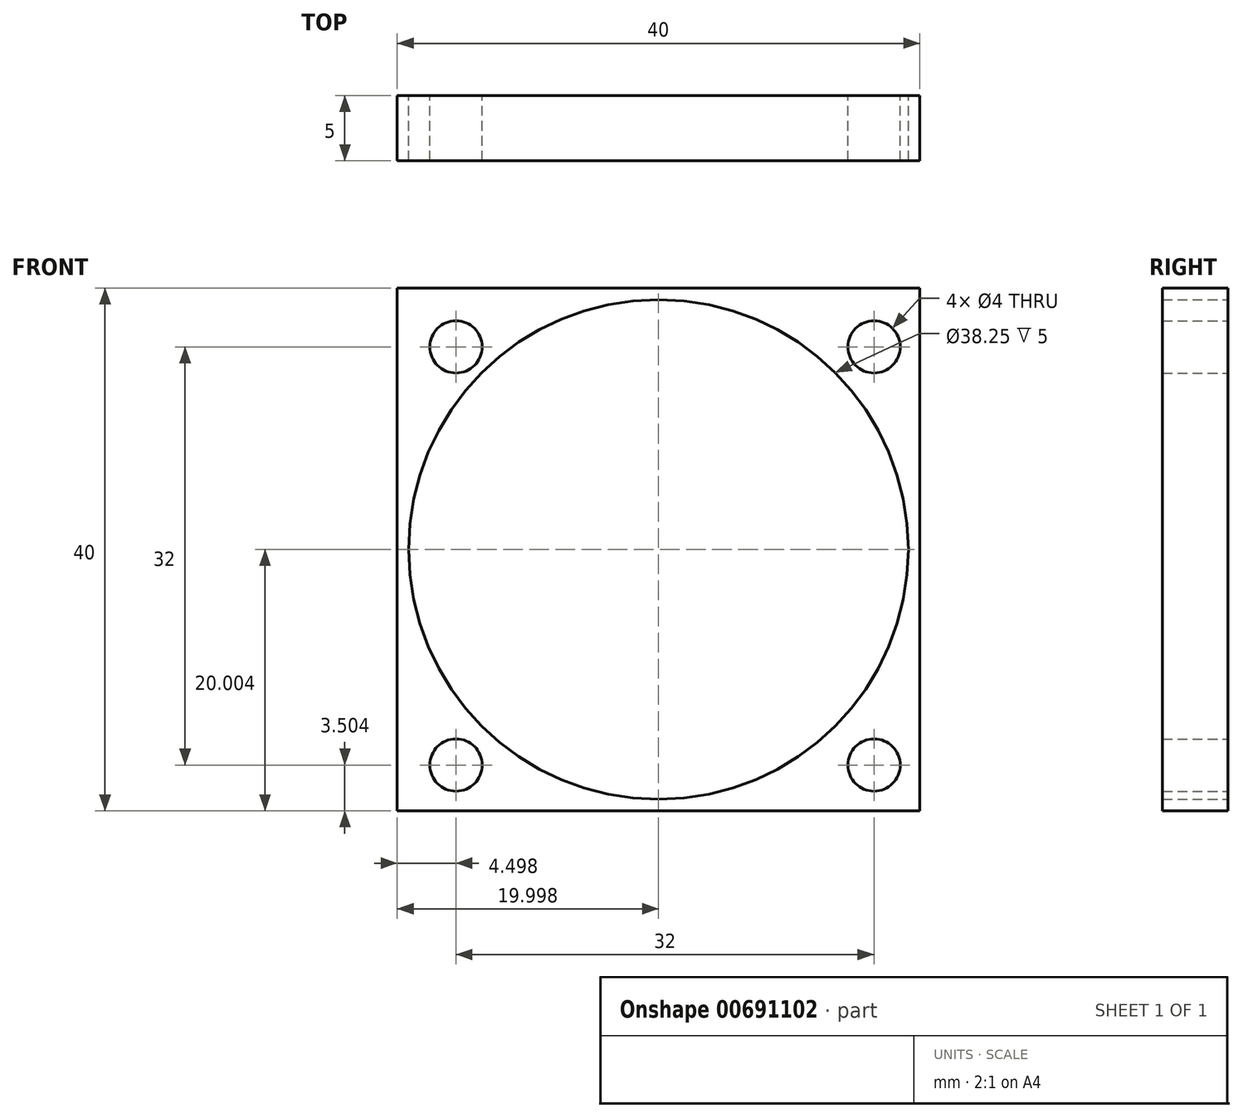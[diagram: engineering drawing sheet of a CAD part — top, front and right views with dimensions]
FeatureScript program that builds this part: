
annotation { "Feature Type Name" : "Feature", "Feature Type Description" : "" }
export const myFeature = defineFeature(function(context is Context, id is Id, definition is map)
    precondition{}
    {
        {
            var Q0;
            Q0=qCreatedBy(makeId("Front.planeOp"),FACE);
            var sketch = newSketch(context, id + "F0", { "sketchPlane" : qUnion([Q0])});
            skLineSegment(sketch, "E0.bottom", {"start": v(-27.87, 25.17) * mm, "end": v(12.13, 25.17) * mm});
            skLineSegment(sketch, "E0.top", {"start": v(-27.87, -14.83) * mm, "end": v(12.13, -14.83) * mm});
            skLineSegment(sketch, "E0.left", {"start": v(-27.87, 25.17) * mm, "end": v(-27.87, -14.83) * mm});
            skLineSegment(sketch, "E0.right", {"start": v(12.13, 25.17) * mm, "end": v(12.13, -14.83) * mm});
            skCircle(sketch, "E1", {"center": v(-23.37, 20.67) * mm, "radius": 2 * mm});
            skCircle(sketch, "E2", {"center": v(8.63, 20.67) * mm, "radius": 2 * mm});
            skCircle(sketch, "E3", {"center": v(8.63, -11.33) * mm, "radius": 2 * mm});
            skCircle(sketch, "E4", {"center": v(-23.37, -11.33) * mm, "radius": 2 * mm});
            skCircle(sketch, "E5", {"center": v(-7.87, 5.17) * mm, "radius": 19.12 * mm});
            skSolve(sketch);
        }
        {
            var Q0;
            Q0 = qSketchRegion(id + "F0", true);
            extrude(context, id + "F1", {"entities" : qUnion([Q0]), "depth" : 5 * mm, "offsetDistance" : 25 * mm});
        }
    });
